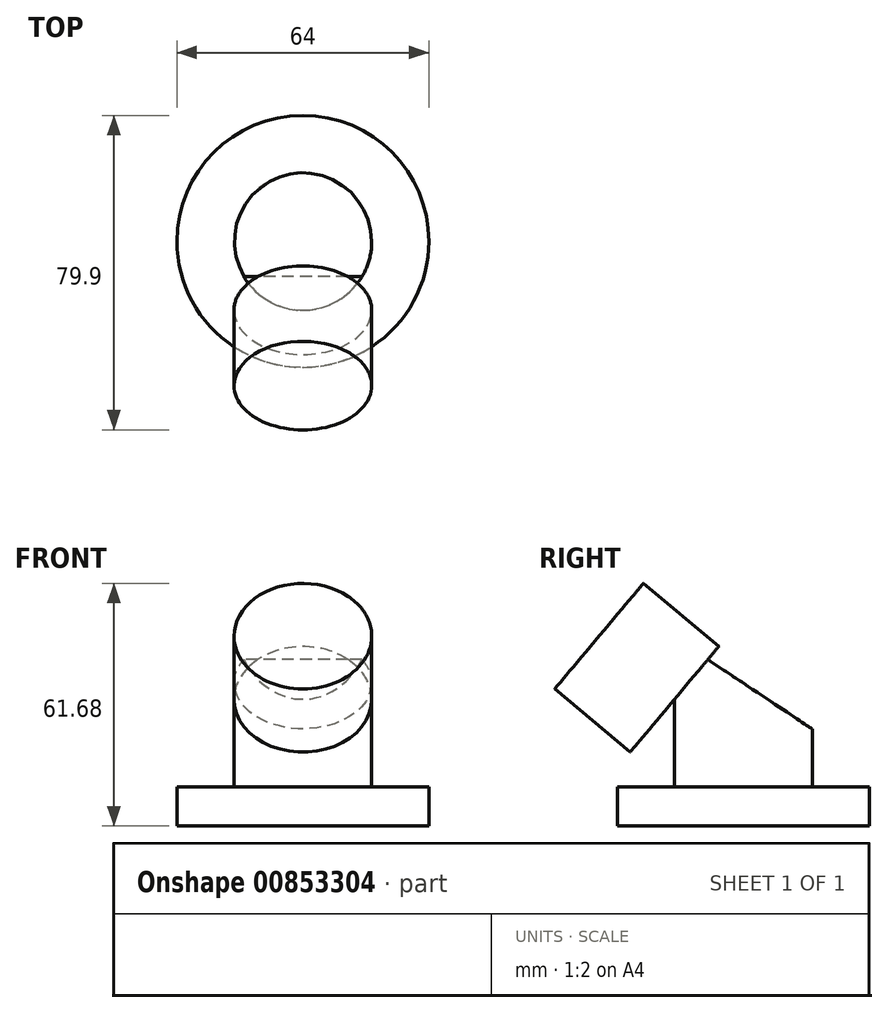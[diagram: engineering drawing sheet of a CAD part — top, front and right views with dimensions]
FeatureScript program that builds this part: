
annotation { "Feature Type Name" : "Feature", "Feature Type Description" : "" }
export const myFeature = defineFeature(function(context is Context, id is Id, definition is map)
    precondition{}
    {
        {
            var Q0;
            Q0=qCreatedBy(makeId("Right.planeOp"),FACE);
            var sketch = newSketch(context, id + "F0", { "sketchPlane" : qUnion([Q0])});
            skLineSegment(sketch, "E0.bottom", {"start": v(32, 0) * mm, "end": v(-32, 0) * mm});
            skLineSegment(sketch, "E0.top", {"start": v(32, 15) * mm, "end": v(-32, 15) * mm});
            skLineSegment(sketch, "E0.left", {"start": v(32, 0) * mm, "end": v(32, 15) * mm});
            skLineSegment(sketch, "E0.right", {"start": v(-32, 0) * mm, "end": v(-32, 15) * mm});
            skLineSegment(sketch, "E1.bottom", {"start": v(32, 15) * mm, "end": v(-31.93, 15) * mm});
            skLineSegment(sketch, "E1.top", {"start": v(32, 56.94) * mm, "end": v(-31.93, 56.94) * mm});
            skLineSegment(sketch, "E1.left", {"start": v(32, 15) * mm, "end": v(32, 56.94) * mm});
            skLineSegment(sketch, "E1.right", {"start": v(-31.93, 15) * mm, "end": v(-31.93, 56.94) * mm});
            skLineSegment(sketch, "E2", {"start": v(-31.93, 15) * mm, "end": v(-9, 42.33) * mm});
            skLineSegment(sketch, "E3", {"start": v(-31.93, 15) * mm, "end": v(-3.16, 15) * mm});
            skLineSegment(sketch, "E4", {"start": v(-9, 42.33) * mm, "end": v(32, 15) * mm});
            skSolve(sketch);
        }
        {
            var Q0;
            {var subQ3=sQuery(id+"F0.wireOp",EDGE,"E2");Q0=makeQuery(id+"F0.imprint","IMPRINT",FACE,{"disambiguationData":[TD([[makeQuery(id+"F0.imprint","IMPRINT",EDGE,{"derivedFrom":subQ3}),-1.0]])]});}
            var Q1;
            Q1=makeQuery(id+"F0.imprint","IMPRINT",FACE,{"disambiguationData":[TD([[makeQuery(id+"F0.imprint","IMPRINT",EDGE,{"derivedFrom":sQuery(id+"F0.wireOp",EDGE,"E0.bottom")}),-1.0]])]});
            extrude(context, id + "F1", {"entities" : qUnion([Q0, Q1]), "endBound" : BoundingType.SYMMETRIC, "depth" : 64 * mm, "offsetDistance" : 25 * mm});
        }
        {
            var Q0;
            Q0=makeQuery(id+"F1.opExtrude","SWEPT_FACE",FACE,{"disambiguationData":[OSD([sQuery(id+"F0.wireOp",EDGE,"E0.bottom")])]});
            var sketch = newSketch(context, id + "F2", { "sketchPlane" : qUnion([Q0])});
            skCircle(sketch, "E5", {"center": v(0, 0) * mm, "radius": 32 * mm});
            skSolve(sketch);
        }
        {
            var Q0;
            {var subQ0=sQuery(id+"F2.wireOp",EDGE,"E5");var subQ1=sQuery(id+"F0.wireOp",EDGE,"E0.bottom");var subQ4=makeQuery(id+"F1.opExtrude","CAP_EDGE",EDGE,{"disambiguationData":[OSD([subQ1])],"isStart":true});var subQ5=makeQuery(id+"F2.imprint","INTERSECT",VERTEX,{"derivedFrom":[subQ4,subQ0]});Q0=makeQuery(id+"F2.imprint","IMPRINT",FACE,{"disambiguationData":[TD([[makeQuery(id+"F2.imprint","IMPRINT",EDGE,{"disambiguationData":[TD([[subQ5,1.0]])],"derivedFrom":subQ0}),-1.0]])]});}
            var Q1;
            {var subQ0=sQuery(id+"F2.wireOp",EDGE,"E5");var subQ1=sQuery(id+"F0.wireOp",EDGE,"E0.bottom");var subQ4=makeQuery(id+"F1.opExtrude","CAP_EDGE",EDGE,{"disambiguationData":[OSD([subQ1])],"isStart":false});var subQ5=makeQuery(id+"F2.imprint","INTERSECT",VERTEX,{"derivedFrom":[subQ4,subQ0]});Q1=makeQuery(id+"F2.imprint","IMPRINT",FACE,{"disambiguationData":[TD([[makeQuery(id+"F2.imprint","IMPRINT",EDGE,{"disambiguationData":[TD([[subQ5,-1.0]])],"derivedFrom":subQ0}),-1.0]])]});}
            var Q2;
            {var subQ0=sQuery(id+"F2.wireOp",EDGE,"E5");var subQ1=sQuery(id+"F0.wireOp",EDGE,"E0.bottom");var subQ2=makeQuery(id+"F1.opExtrude","CAP_EDGE",EDGE,{"disambiguationData":[OSD([subQ1])],"isStart":false});var subQ3=makeQuery(id+"F2.imprint","INTERSECT",VERTEX,{"derivedFrom":[subQ2,subQ0]});Q2=makeQuery(id+"F2.imprint","IMPRINT",FACE,{"disambiguationData":[TD([[makeQuery(id+"F2.imprint","IMPRINT",EDGE,{"disambiguationData":[TD([[subQ3,1.0]])],"derivedFrom":subQ0}),-1.0]])]});}
            var Q3;
            {var subQ0=sQuery(id+"F2.wireOp",EDGE,"E5");var subQ1=sQuery(id+"F0.wireOp",EDGE,"E0.bottom");var subQ2=makeQuery(id+"F1.opExtrude","CAP_EDGE",EDGE,{"disambiguationData":[OSD([subQ1])],"isStart":true});var subQ3=makeQuery(id+"F2.imprint","INTERSECT",VERTEX,{"derivedFrom":[subQ2,subQ0]});Q3=makeQuery(id+"F2.imprint","IMPRINT",FACE,{"disambiguationData":[TD([[makeQuery(id+"F2.imprint","IMPRINT",EDGE,{"disambiguationData":[TD([[subQ3,-1.0]])],"derivedFrom":subQ0}),-1.0]])]});}
            extrude(context, id + "F3", {"entities" : qUnion([Q0, Q1, Q2, Q3]), "operationType" : NewBodyOperationType.REMOVE, "oppositeDirection" : true, "depth" : 50 * mm, "offsetDistance" : 25 * mm});
        }
        {
            var Q0;
            Q0=qCreatedBy(makeId("Top.planeOp"),FACE);
            cPlane(context, id + "F4", {"entities" : qUnion([Q0]), "cplaneType" : CPlaneType.OFFSET, "offset" : 50 * mm, "width" : 150 * mm, "height" : 150 * mm});
        }
        {
            var Q0;
            Q0=qCreatedBy(id+"F4.planeOp",FACE);
            var sketch = newSketch(context, id + "F5", { "sketchPlane" : qUnion([Q0])});
            skCircle(sketch, "E6", {"center": v(0, 0) * mm, "radius": 17.5 * mm});
            skCircle(sketch, "E7", {"center": v(0, 0) * mm, "radius": 32 * mm});
            skSolve(sketch);
        }
        {
            var Q0;
            Q0=makeQuery(id+"F5.imprint","IMPRINT",FACE,{"disambiguationData":[TD([[makeQuery(id+"F5.imprint","IMPRINT",EDGE,{"derivedFrom":sQuery(id+"F5.wireOp",EDGE,"E6")}),-1.0]])]});
            extrude(context, id + "F6", {"entities" : qUnion([Q0]), "operationType" : NewBodyOperationType.REMOVE, "oppositeDirection" : true, "depth" : 40 * mm, "offsetDistance" : 25 * mm});
        }
        {
            var Q0;
            Q0=makeQuery(id+"F1.opExtrude","SWEPT_FACE",FACE,{"disambiguationData":[OSD([sQuery(id+"F0.wireOp",EDGE,"E2")])]});
            var sketch = newSketch(context, id + "F7", { "sketchPlane" : qUnion([Q0])});
            skCircle(sketch, "E8", {"center": v(0, 13.42) * mm, "radius": 17.5 * mm});
            skSolve(sketch);
        }
        {
            var Q0;
            {var subQ0=sQuery(id+"F7.wireOp",EDGE,"E8");var subQ1=makeQuery(id+"F6.boolean.opBoolean","INTERSECT",EDGE,{"derivedFrom":[makeQuery(id+"F1.opExtrude","SWEPT_FACE",FACE,{"disambiguationData":[OSD([sQuery(id+"F0.wireOp",EDGE,"E2")])]}),makeQuery(id+"F6.opExtrude","SWEPT_FACE",FACE,{"disambiguationData":[OSD([sQuery(id+"F5.wireOp",EDGE,"E6")])]})]});var subQ2=makeQuery(id+"F7.imprint","INTERSECT",VERTEX,{"disambiguationData":[OD(0.0)],"derivedFrom":[subQ1,subQ0]});Q0=makeQuery(id+"F7.imprint","IMPRINT",FACE,{"disambiguationData":[TD([[makeQuery(id+"F7.imprint","IMPRINT",EDGE,{"disambiguationData":[TD([[subQ2,1.0]])],"derivedFrom":subQ0}),1.0]])]});}
            var Q1;
            {var subQ0=sQuery(id+"F7.wireOp",EDGE,"E8");var subQ1=sQuery(id+"F0.wireOp",EDGE,"E2");var subQ2=makeQuery(id+"F1.opExtrude","SWEPT_EDGE",EDGE,{"disambiguationData":[OSD([subQ1,sQuery(id+"F0.wireOp",EDGE,"E4")])]});var subQ3=makeQuery(id+"F7.imprint","INTERSECT",VERTEX,{"disambiguationData":[OD(0.0)],"derivedFrom":[subQ2,subQ0]});Q1=makeQuery(id+"F7.imprint","IMPRINT",FACE,{"disambiguationData":[TD([[makeQuery(id+"F7.imprint","IMPRINT",EDGE,{"disambiguationData":[TD([[subQ3,1.0]])],"derivedFrom":subQ0}),1.0]])]});}
            var Q2;
            {var subQ0=sQuery(id+"F7.wireOp",EDGE,"E8");var subQ1=makeQuery(id+"F1.opExtrude","SWEPT_EDGE",EDGE,{"disambiguationData":[OSD([sQuery(id+"F0.wireOp",EDGE,"E2"),sQuery(id+"F0.wireOp",EDGE,"E4")])]});var subQ2=makeQuery(id+"F7.imprint","INTERSECT",VERTEX,{"disambiguationData":[OD(0.0)],"derivedFrom":[subQ1,subQ0]});Q2=makeQuery(id+"F7.imprint","IMPRINT",FACE,{"disambiguationData":[TD([[makeQuery(id+"F7.imprint","IMPRINT",EDGE,{"disambiguationData":[TD([[subQ2,-1.0]])],"derivedFrom":subQ0}),1.0]])]});}
            extrude(context, id + "F8", {"entities" : qUnion([Q0, Q1, Q2]), "operationType" : NewBodyOperationType.ADD, "depth" : 25 * mm, "offsetDistance" : 25 * mm});
        }
    });
